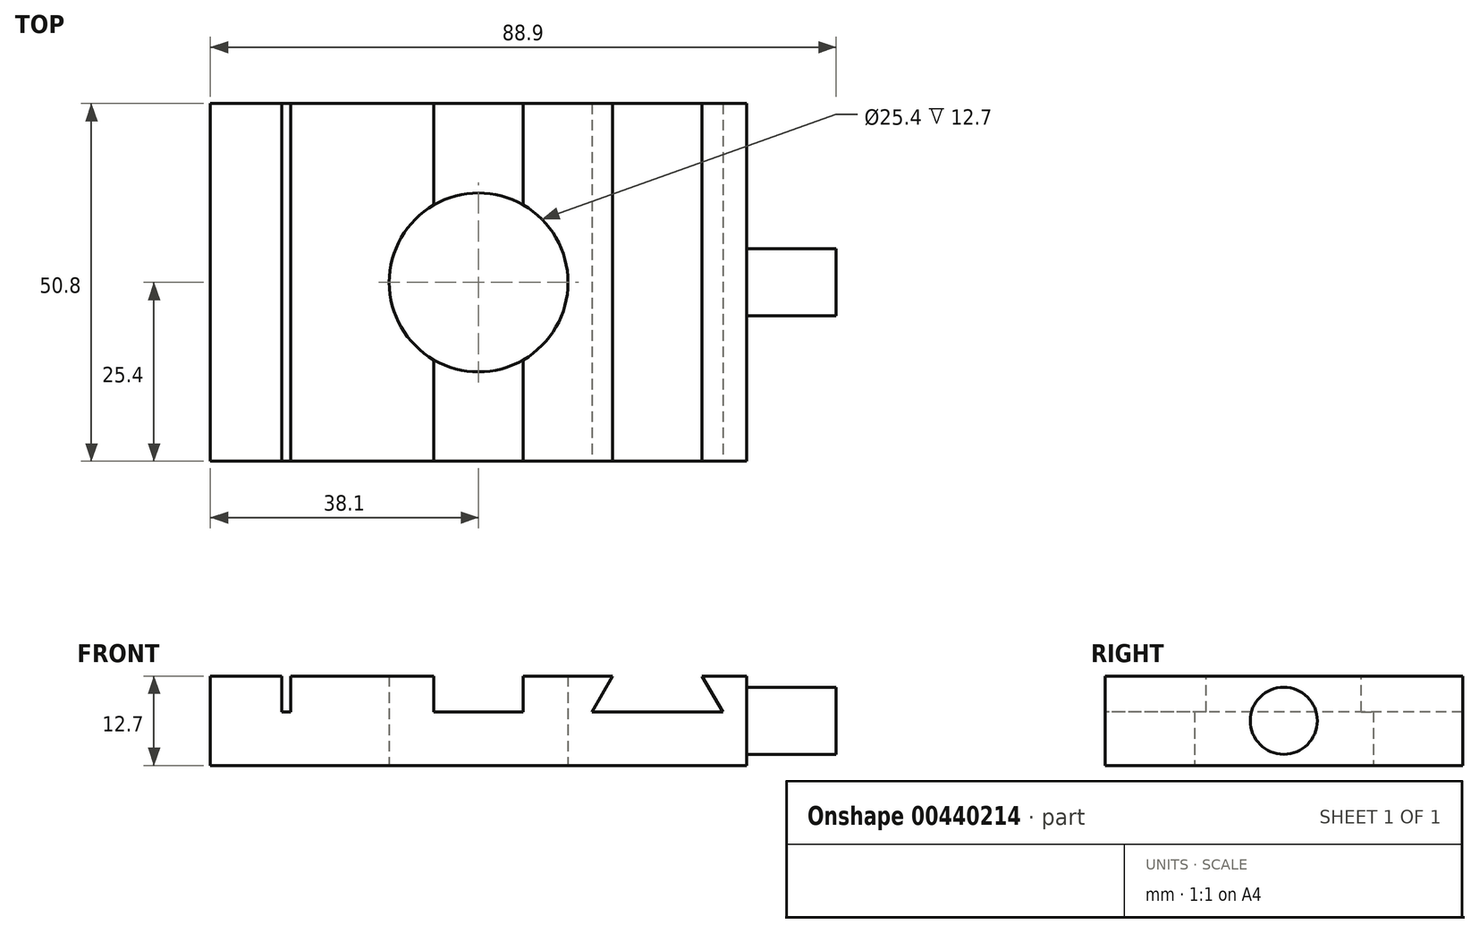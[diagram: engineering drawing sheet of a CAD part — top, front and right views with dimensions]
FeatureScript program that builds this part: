
annotation { "Feature Type Name" : "Feature", "Feature Type Description" : "" }
export const myFeature = defineFeature(function(context is Context, id is Id, definition is map)
    precondition{}
    {
        {
            var Q0;
            Q0=qCreatedBy(makeId("Top.planeOp"),FACE);
            var sketch = newSketch(context, id + "F0", { "sketchPlane" : qUnion([Q0])});
            skLineSegment(sketch, "E0.bottom", {"start": v(38.1, 25.4) * mm, "end": v(-38.1, 25.4) * mm});
            skLineSegment(sketch, "E0.top", {"start": v(38.1, -25.4) * mm, "end": v(-38.1, -25.4) * mm});
            skLineSegment(sketch, "E0.left", {"start": v(38.1, 25.4) * mm, "end": v(38.1, -25.4) * mm});
            skLineSegment(sketch, "E0.right", {"start": v(-38.1, 25.4) * mm, "end": v(-38.1, -25.4) * mm});
            skPoint(sketch, "E0.middle", {"position": v(0, 0) * mm});
            skCircle(sketch, "E1", {"center": v(0, 0) * mm, "radius": 12.7 * mm});
            skSolve(sketch);
        }
        {
            var Q0;
            Q0=makeQuery(id+"F0.imprint","IMPRINT",FACE,{"disambiguationData":[TD([[makeQuery(id+"F0.imprint","IMPRINT",EDGE,{"derivedFrom":sQuery(id+"F0.wireOp",EDGE,"E0.bottom")}),1.0]])]});
            extrude(context, id + "F1", {"entities" : qUnion([Q0]), "depth" : 12.7 * mm});
        }
        {
            var Q0;
            Q0=makeQuery(id+"F1.opExtrude","CAP_FACE",FACE,{"disambiguationData":[OSD([sQuery(id+"F0.wireOp",EDGE,"E0.bottom"),sQuery(id+"F0.wireOp",EDGE,"E0.top"),sQuery(id+"F0.wireOp",EDGE,"E0.left"),sQuery(id+"F0.wireOp",EDGE,"E0.right"),sQuery(id+"F0.wireOp",EDGE,"E1")])],"isStart":false});
            var sketch = newSketch(context, id + "F2", { "sketchPlane" : qUnion([Q0])});
            skLineSegment(sketch, "E2.bottom", {"start": v(-27.94, 25.4) * mm, "end": v(-26.67, 25.4) * mm});
            skLineSegment(sketch, "E2.top", {"start": v(-27.94, -25.4) * mm, "end": v(-26.67, -25.4) * mm});
            skLineSegment(sketch, "E2.left", {"start": v(-27.94, 25.4) * mm, "end": v(-27.94, -25.4) * mm});
            skLineSegment(sketch, "E2.right", {"start": v(-26.67, 25.4) * mm, "end": v(-26.67, -25.4) * mm});
            skLineSegment(sketch, "E3", {"start": v(-6.35, 25.4) * mm, "end": v(-6.35, -25.4) * mm});
            skLineSegment(sketch, "E4", {"start": v(-6.35, -25.4) * mm, "end": v(6.35, -25.4) * mm});
            skLineSegment(sketch, "E5", {"start": v(6.35, -25.4) * mm, "end": v(6.35, 25.4) * mm});
            skLineSegment(sketch, "E6", {"start": v(6.35, 25.4) * mm, "end": v(-6.35, 25.4) * mm});
            skPoint(sketch, "E7", {"position": v(0, 0) * mm});
            skLineSegment(sketch, "E8", {"start": v(0, 25.4) * mm, "end": v(0, -25.4) * mm, "construction": true});
            skSolve(sketch);
        }
        {
            var Q0;
            Q0=makeQuery(id+"F2.imprint","IMPRINT",FACE,{"disambiguationData":[TD([[makeQuery(id+"F2.imprint","IMPRINT",EDGE,{"derivedFrom":sQuery(id+"F2.wireOp",EDGE,"E2.bottom")}),1.0]])]});
            var Q1;
            {var subQ0=sQuery(id+"F2.wireOp",EDGE,"E4");Q1=makeQuery(id+"F2.imprint","IMPRINT",FACE,{"disambiguationData":[TD([[makeQuery(id+"F2.imprint","IMPRINT",EDGE,{"derivedFrom":subQ0}),-1.0]])]});}
            var Q2;
            {var subQ0=sQuery(id+"F2.wireOp",EDGE,"E6");Q2=makeQuery(id+"F2.imprint","IMPRINT",FACE,{"disambiguationData":[TD([[makeQuery(id+"F2.imprint","IMPRINT",EDGE,{"derivedFrom":subQ0}),1.0]])]});}
            extrude(context, id + "F3", {"entities" : qUnion([Q0, Q1, Q2]), "operationType" : NewBodyOperationType.REMOVE, "oppositeDirection" : true, "depth" : 5.08 * mm});
        }
        {
            var Q0;
            Q0=makeQuery(id+"F1.opExtrude","SWEPT_FACE",FACE,{"disambiguationData":[OSD([sQuery(id+"F0.wireOp",EDGE,"E0.top")])]});
            var sketch = newSketch(context, id + "F4", { "sketchPlane" : qUnion([Q0])});
            skLineSegment(sketch, "E9", {"start": v(19.05, 12.7) * mm, "end": v(16.12, 7.62) * mm});
            skLineSegment(sketch, "E10", {"start": v(16.12, 7.62) * mm, "end": v(34.68, 7.62) * mm});
            skLineSegment(sketch, "E11", {"start": v(34.68, 7.62) * mm, "end": v(31.75, 12.7) * mm});
            skLineSegment(sketch, "E12", {"start": v(31.75, 12.7) * mm, "end": v(19.05, 12.7) * mm});
            skLineSegment(sketch, "E13", {"start": v(25.4, 7.62) * mm, "end": v(25.4, 12.7) * mm, "construction": true});
            skSolve(sketch);
        }
        {
            var Q0;
            Q0=makeQuery(id+"F4.imprint","IMPRINT",FACE,{"disambiguationData":[TD([[makeQuery(id+"F4.imprint","IMPRINT",EDGE,{"derivedFrom":sQuery(id+"F4.wireOp",EDGE,"E9")}),1.0]])]});
            extrude(context, id + "F5", {"entities" : qUnion([Q0]), "operationType" : NewBodyOperationType.REMOVE, "endBound" : BoundingType.THROUGH_ALL, "oppositeDirection" : true, "depth" : 25.4 * mm});
        }
        {
            var Q0;
            Q0=makeQuery(id+"F1.opExtrude","SWEPT_FACE",FACE,{"disambiguationData":[OSD([sQuery(id+"F0.wireOp",EDGE,"E0.left")])]});
            var sketch = newSketch(context, id + "F6", { "sketchPlane" : qUnion([Q0])});
            skCircle(sketch, "E14", {"center": v(0, 6.35) * mm, "radius": 4.76 * mm});
            skPoint(sketch, "E14.centerSnap0", {"position": v(-25.4, 6.35) * mm});
            skPoint(sketch, "E14.centerSnap1", {"position": v(0, 12.7) * mm});
            skSolve(sketch);
        }
        {
            var Q0;
            Q0=makeQuery(id+"F6.imprint","IMPRINT",FACE,{"disambiguationData":[TD([[makeQuery(id+"F6.imprint","IMPRINT",EDGE,{"derivedFrom":sQuery(id+"F6.wireOp",EDGE,"E14")}),1.0]])]});
            extrude(context, id + "F7", {"entities" : qUnion([Q0]), "operationType" : NewBodyOperationType.ADD, "depth" : 12.7 * mm});
        }
    });
